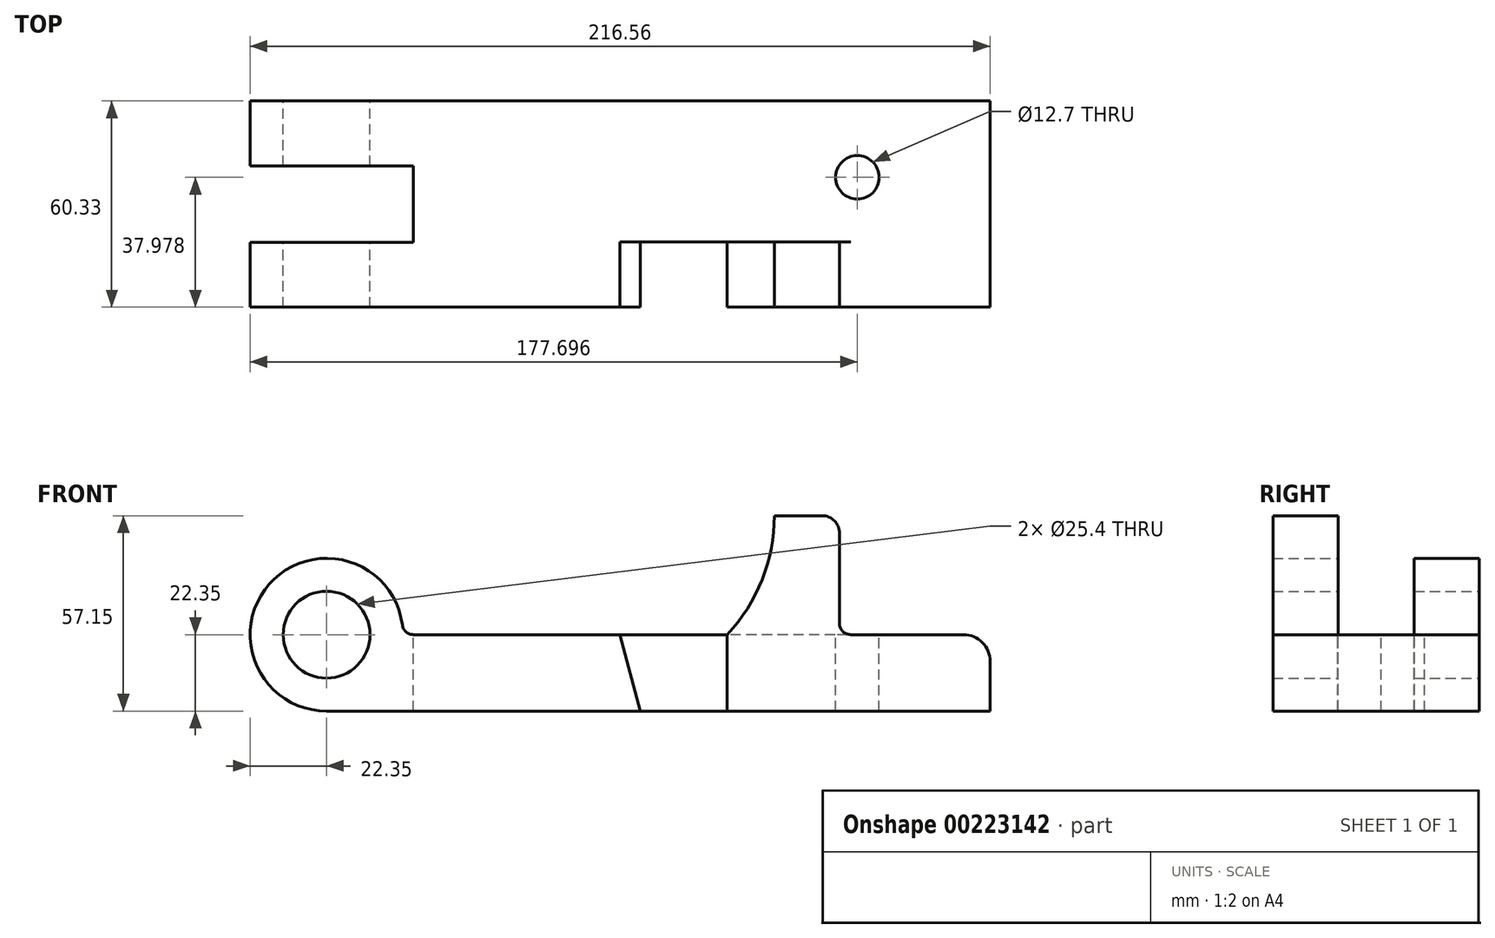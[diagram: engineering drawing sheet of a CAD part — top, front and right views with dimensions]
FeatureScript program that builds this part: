
annotation { "Feature Type Name" : "Feature", "Feature Type Description" : "" }
export const myFeature = defineFeature(function(context is Context, id is Id, definition is map)
    precondition{}
    {
        {
            var Q0;
            Q0=qCreatedBy(makeId("Front.planeOp"),FACE);
            var sketch = newSketch(context, id + "F0", { "sketchPlane" : qUnion([Q0])});
            skCircle(sketch, "E0", {"center": v(0, 0) * mm, "radius": 12.7 * mm});
            skArc(sketch, "E1", {"start": v(22.17, 2.88) * mm, "mid": v(-16.8, 14.75) * mm, "end": v(0, -22.35) * mm});
            skLineSegment(sketch, "E2", {"start": v(0, -22.35) * mm, "end": v(194.2, -22.35) * mm});
            skLineSegment(sketch, "E3", {"start": v(25.44, 0) * mm, "end": v(117.25, 0) * mm});
            skLineSegment(sketch, "E4", {"start": v(91.85, -22.35) * mm, "end": v(85.85, 0) * mm});
            skLineSegment(sketch, "E5", {"start": v(194.2, -22.35) * mm, "end": v(194.2, -7.87) * mm});
            skLineSegment(sketch, "E6", {"start": v(0, 34.8) * mm, "end": v(145, 34.8) * mm});
            skLineSegment(sketch, "E7", {"start": v(0, 34.8) * mm, "end": v(131.04, 34.8) * mm});
            skArc(sketch, "E8", {"start": v(117.25, 0) * mm, "mid": v(127.46, 16.08) * mm, "end": v(131.04, 34.8) * mm});
            skLineSegment(sketch, "E9", {"start": v(153.4, 0) * mm, "end": v(186.33, 0) * mm});
            skLineSegment(sketch, "E10", {"start": v(150.09, 29.72) * mm, "end": v(150.09, 3.3) * mm});
            skLineSegment(sketch, "E11", {"start": v(117.25, 0) * mm, "end": v(117.25, -22.35) * mm});
            skPoint(sketch, "E12.visualSharp", {"position": v(150.09, 0) * mm});
            skArc(sketch, "E12.filletArc", {"start": v(150.09, 3.3) * mm, "mid": v(151.06, 0.97) * mm, "end": v(153.4, 0) * mm});
            skPoint(sketch, "E13.visualSharp", {"position": v(150.09, 34.8) * mm});
            skArc(sketch, "E13.filletArc", {"start": v(150.09, 29.72) * mm, "mid": v(148.6, 33.31) * mm, "end": v(145, 34.8) * mm});
            skPoint(sketch, "E14.visualSharp", {"position": v(194.2, 0) * mm});
            skArc(sketch, "E14.filletArc", {"start": v(194.2, -7.87) * mm, "mid": v(191.9, -2.3) * mm, "end": v(186.33, 0) * mm});
            skPoint(sketch, "E15.visualSharp", {"position": v(22.35, 0) * mm});
            skArc(sketch, "E15.filletArc", {"start": v(22.17, 2.88) * mm, "mid": v(23.26, 0.82) * mm, "end": v(25.44, 0) * mm});
            skLineSegment(sketch, "E16", {"start": v(0, 0) * mm, "end": v(-22.35, 0) * mm});
            skSolve(sketch);
        }
        {
            var Q0;
            {var subQ0=sQuery(id+"F0.wireOp",EDGE,"E5");Q0=makeQuery(id+"F0.imprint","IMPRINT",FACE,{"disambiguationData":[TD([[makeQuery(id+"F0.imprint","IMPRINT",EDGE,{"derivedFrom":subQ0}),1.0]])]});}
            var Q1;
            {var subQ0=sQuery(id+"F0.wireOp",EDGE,"E4");Q1=makeQuery(id+"F0.imprint","IMPRINT",FACE,{"disambiguationData":[TD([[makeQuery(id+"F0.imprint","IMPRINT",EDGE,{"derivedFrom":subQ0}),-1.0]])]});}
            var Q2;
            Q2=makeQuery(id+"F0.imprint","IMPRINT",FACE,{"disambiguationData":[TD([[makeQuery(id+"F0.imprint","IMPRINT",EDGE,{"derivedFrom":sQuery(id+"F0.wireOp",EDGE,"E0")}),-1.0]])]});
            extrude(context, id + "F1", {"entities" : qUnion([Q0, Q1, Q2]), "depth" : 60.32 * mm});
        }
        {
            var Q0;
            Q0=makeQuery(id+"F1.opExtrude","SWEPT_FACE",FACE,{"disambiguationData":[OSD([sQuery(id+"F0.wireOp",EDGE,"E3")])]});
            var sketch = newSketch(context, id + "F2", { "sketchPlane" : qUnion([Q0])});
            skLineSegment(sketch, "E17.0", {"start": v(22.35, -60.33) * mm, "end": v(117.25, -60.33) * mm});
            skLineSegment(sketch, "E18", {"start": v(-23.99, -19) * mm, "end": v(25.44, -19) * mm});
            skLineSegment(sketch, "E19", {"start": v(-23.27, -41.33) * mm, "end": v(25.44, -41.33) * mm});
            skLineSegment(sketch, "E20", {"start": v(25.44, -19) * mm, "end": v(25.44, -41.33) * mm});
            skLineSegment(sketch, "E21", {"start": v(-23.99, -19) * mm, "end": v(-23.99, -41.33) * mm});
            skLineSegment(sketch, "E22", {"start": v(-23.99, -41.33) * mm, "end": v(-23.27, -41.33) * mm});
            skSolve(sketch);
        }
        {
            var Q0;
            Q0 = qSketchRegion(id + "F2", true);
            extrude(context, id + "F3", {"entities" : qUnion([Q0]), "operationType" : NewBodyOperationType.REMOVE, "endBound" : BoundingType.SYMMETRIC, "oppositeDirection" : true, "depth" : 127.5 * mm});
        }
        {
            var Q0;
            Q0=makeQuery(id+"F1.opExtrude","SWEPT_FACE",FACE,{"disambiguationData":[OSD([sQuery(id+"F0.wireOp",EDGE,"E6")])]});
            var sketch = newSketch(context, id + "F4", { "sketchPlane" : qUnion([Q0])});
            skLineSegment(sketch, "E23", {"start": v(91.7, -60.33) * mm, "end": v(153.4, -60.33) * mm});
            skLineSegment(sketch, "E24", {"start": v(153.4, -60.33) * mm, "end": v(153.4, -41.28) * mm});
            skLineSegment(sketch, "E25", {"start": v(153.4, -41.27) * mm, "end": v(91.7, -41.27) * mm});
            skLineSegment(sketch, "E26", {"start": v(91.7, -41.28) * mm, "end": v(91.7, -60.33) * mm});
            skLineSegment(sketch, "E27.0", {"start": v(153.4, -60.33) * mm, "end": v(153.4, 0) * mm});
            skLineSegment(sketch, "E28", {"start": v(91.7, -41.27) * mm, "end": v(91.7, 0) * mm});
            skLineSegment(sketch, "E29", {"start": v(91.7, 0) * mm, "end": v(153.4, 0) * mm});
            skSolve(sketch);
        }
        {
            var Q0;
            {var subQ0=sQuery(id+"F4.wireOp",EDGE,"E28");Q0=makeQuery(id+"F4.imprint","IMPRINT",FACE,{"disambiguationData":[TD([[makeQuery(id+"F4.imprint","IMPRINT",EDGE,{"derivedFrom":subQ0}),-1.0]])]});}
            var Q1;
            {var subQ0=sQuery(id+"F4.wireOp",EDGE,"E25");var subQ1=sQuery(id+"F0.wireOp",EDGE,"E6");var subQ2=makeQuery(id+"F1.opExtrude","SWEPT_EDGE",EDGE,{"disambiguationData":[OSD([subQ1,sQuery(id+"F0.wireOp",EDGE,"E13.filletArc")])]});var subQ3=makeQuery(id+"F4.imprint","INTERSECT",VERTEX,{"derivedFrom":[subQ2,subQ0]});Q1=makeQuery(id+"F4.imprint","IMPRINT",FACE,{"disambiguationData":[TD([[makeQuery(id+"F4.imprint","IMPRINT",EDGE,{"disambiguationData":[TD([[subQ3,-1.0]])],"derivedFrom":subQ0}),-1.0]])]});}
            var Q2;
            {var subQ0=sQuery(id+"F4.wireOp",EDGE,"E27.0");var subQ1=sQuery(id+"F4.wireOp",EDGE,"E25");var subQ2=makeQuery(id+"F4.imprint","INTERSECT",VERTEX,{"derivedFrom":[subQ1,subQ0]});Q2=makeQuery(id+"F4.imprint","IMPRINT",FACE,{"disambiguationData":[TD([[makeQuery(id+"F4.imprint","IMPRINT",EDGE,{"disambiguationData":[TD([[subQ2,-1.0]])],"derivedFrom":subQ0}),1.0]])]});}
            extrude(context, id + "F5", {"entities" : qUnion([Q0, Q1, Q2]), "operationType" : NewBodyOperationType.REMOVE, "oppositeDirection" : true, "depth" : 34.8 * mm});
        }
        {
            var Q0;
            Q0=makeQuery(id+"F5.boolean.opBoolean","MERGE",FACE,{"derivedFrom":[makeQuery(id+"F1.opExtrude","SWEPT_FACE",FACE,{"disambiguationData":[OSD([sQuery(id+"F0.wireOp",EDGE,"E3")])]}),makeQuery(id+"F1.opExtrude","SWEPT_FACE",FACE,{"disambiguationData":[OSD([sQuery(id+"F0.wireOp",EDGE,"E9")])]}),makeQuery(id+"F5.opExtrude","CAP_FACE",FACE,{"disambiguationData":[OSD([sQuery(id+"F4.wireOp",EDGE,"E25"),sQuery(id+"F4.wireOp",EDGE,"E27.0"),sQuery(id+"F4.wireOp",EDGE,"E28"),sQuery(id+"F4.wireOp",EDGE,"E29")])],"isStart":false})]});
            var sketch = newSketch(context, id + "F6", { "sketchPlane" : qUnion([Q0])});
            skLineSegment(sketch, "E30.0", {"start": v(25.44, 0) * mm, "end": v(186.33, 0) * mm});
            skPoint(sketch, "E31.0", {"position": v(191.9, 0) * mm});
            skLineSegment(sketch, "E32.0", {"start": v(194.2, 0) * mm, "end": v(186.33, 0) * mm});
            skLineSegment(sketch, "E33", {"start": v(194.2, 0) * mm, "end": v(155.35, 0) * mm});
            skLineSegment(sketch, "E34", {"start": v(194.2, 0) * mm, "end": v(194.2, -22.35) * mm});
            skLineSegment(sketch, "E35", {"start": v(155.35, 0) * mm, "end": v(155.35, -22.35) * mm});
            skCircle(sketch, "E36", {"center": v(155.35, -22.35) * mm, "radius": 6.35 * mm});
            skSolve(sketch);
        }
        {
            var Q0;
            Q0 = qSketchRegion(id + "F6", true);
            extrude(context, id + "F7", {"entities" : qUnion([Q0]), "operationType" : NewBodyOperationType.REMOVE, "endBound" : BoundingType.THROUGH_ALL, "oppositeDirection" : true, "depth" : 25.4 * mm});
        }
        {
            var Q0;
            Q0=makeQuery(id+"F1.opExtrude","CAP_FACE",FACE,{"disambiguationData":[OSD([sQuery(id+"F0.wireOp",EDGE,"E0"),sQuery(id+"F0.wireOp",EDGE,"E1"),sQuery(id+"F0.wireOp",EDGE,"E2"),sQuery(id+"F0.wireOp",EDGE,"E3"),sQuery(id+"F0.wireOp",EDGE,"E5"),sQuery(id+"F0.wireOp",EDGE,"E6"),sQuery(id+"F0.wireOp",EDGE,"E8"),sQuery(id+"F0.wireOp",EDGE,"E9"),sQuery(id+"F0.wireOp",EDGE,"E10"),sQuery(id+"F0.wireOp",EDGE,"E12.filletArc"),sQuery(id+"F0.wireOp",EDGE,"E13.filletArc"),sQuery(id+"F0.wireOp",EDGE,"E14.filletArc")])],"isStart":false});
            var sketch = newSketch(context, id + "F8", { "sketchPlane" : qUnion([Q0])});
            skLineSegment(sketch, "E37.0.0", {"start": v(117.25, -22.35) * mm, "end": v(117.25, 0) * mm});
            skLineSegment(sketch, "E37.0.1", {"start": v(117.25, 0) * mm, "end": v(85.85, 0) * mm});
            skLineSegment(sketch, "E37.0.2", {"start": v(85.85, 0) * mm, "end": v(91.85, -22.35) * mm});
            skLineSegment(sketch, "E37.0.3", {"start": v(91.85, -22.35) * mm, "end": v(117.25, -22.35) * mm});
            skSolve(sketch);
        }
        {
            var Q0;
            Q0 = qSketchRegion(id + "F8", true);
            extrude(context, id + "F9", {"entities" : qUnion([Q0]), "operationType" : NewBodyOperationType.REMOVE, "oppositeDirection" : true, "depth" : 19.05 * mm});
        }
    });
